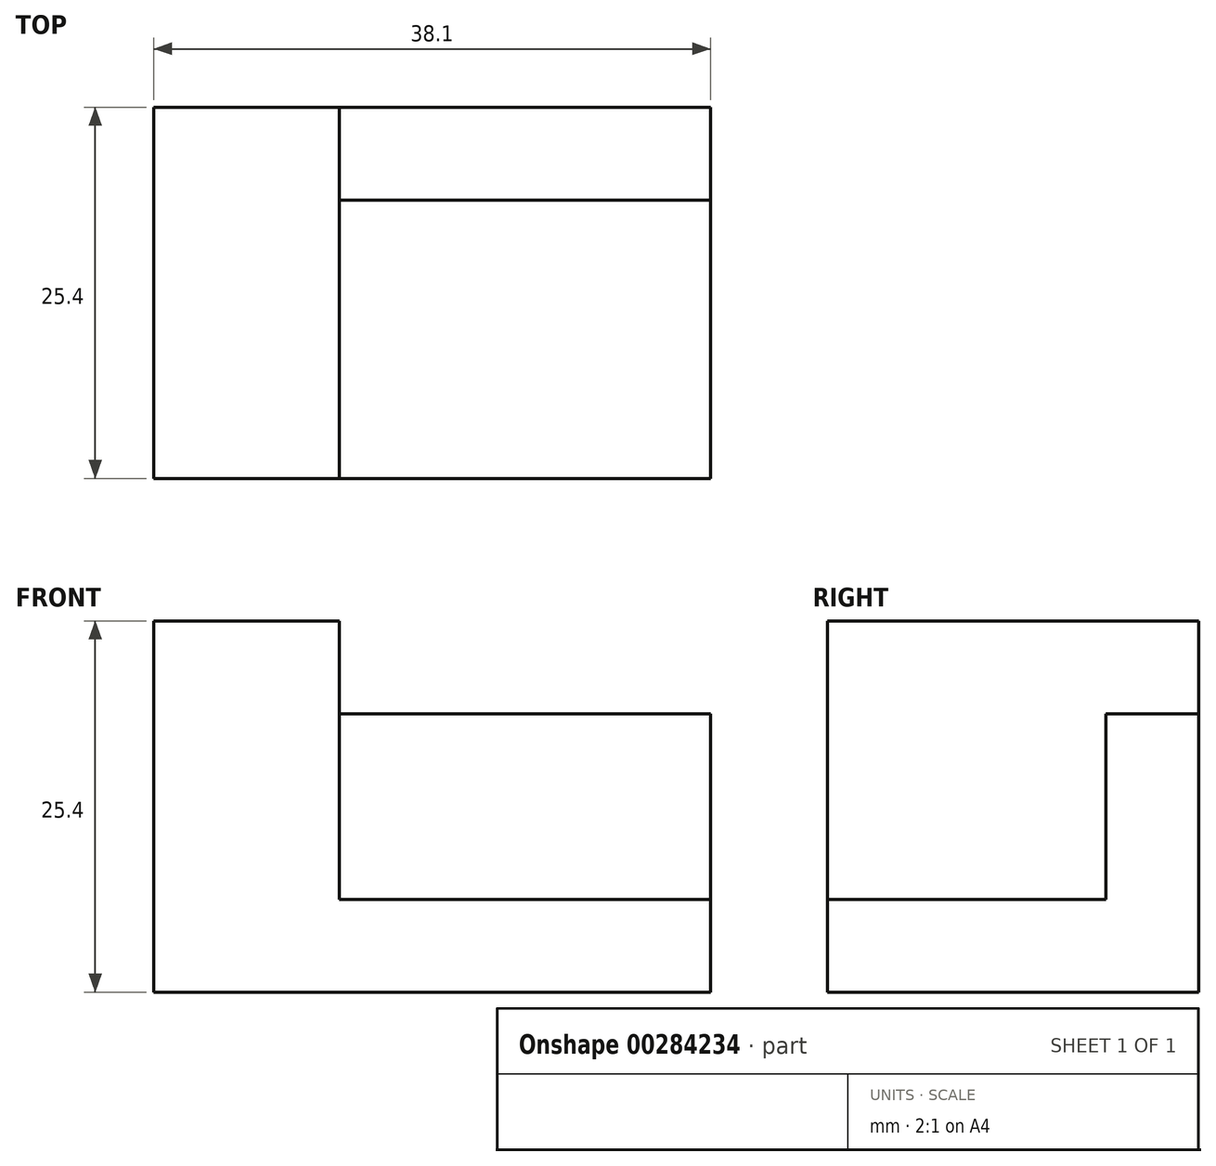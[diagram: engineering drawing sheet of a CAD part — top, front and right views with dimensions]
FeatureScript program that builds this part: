
annotation { "Feature Type Name" : "Feature", "Feature Type Description" : "" }
export const myFeature = defineFeature(function(context is Context, id is Id, definition is map)
    precondition{}
    {
        {
            var Q0;
            Q0=qCreatedBy(makeId("Front.planeOp"),FACE);
            var sketch = newSketch(context, id + "F0", { "sketchPlane" : qUnion([Q0])});
            skLineSegment(sketch, "E0", {"start": v(0, 25.4) * mm, "end": v(0, 0) * mm});
            skLineSegment(sketch, "E1", {"start": v(0, 0) * mm, "end": v(38.1, 0) * mm});
            skLineSegment(sketch, "E2", {"start": v(38.1, 0) * mm, "end": v(38.1, 6.35) * mm});
            skLineSegment(sketch, "E3", {"start": v(38.1, 6.35) * mm, "end": v(12.7, 6.35) * mm});
            skLineSegment(sketch, "E4", {"start": v(12.7, 6.35) * mm, "end": v(12.7, 25.4) * mm});
            skLineSegment(sketch, "E5", {"start": v(12.7, 25.4) * mm, "end": v(0, 25.4) * mm});
            skSolve(sketch);
        }
        {
            var Q0;
            Q0=makeQuery(id+"F0.imprint","IMPRINT",FACE,{"disambiguationData":[TD([[makeQuery(id+"F0.imprint","IMPRINT",EDGE,{"derivedFrom":sQuery(id+"F0.wireOp",EDGE,"E0")}),1.0]])]});
            extrude(context, id + "F1", {"entities" : qUnion([Q0]), "endBound" : BoundingType.SYMMETRIC, "depth" : 25.4 * mm});
        }
        {
            var Q0;
            Q0=makeQuery(id+"F1.opExtrude","SWEPT_FACE",FACE,{"disambiguationData":[OSD([sQuery(id+"F0.wireOp",EDGE,"E3")])]});
            var sketch = newSketch(context, id + "F2", { "sketchPlane" : qUnion([Q0])});
            skLineSegment(sketch, "E6", {"start": v(12.7, 6.35) * mm, "end": v(38.1, 6.35) * mm});
            skLineSegment(sketch, "E7", {"start": v(38.1, 6.35) * mm, "end": v(38.1, 12.7) * mm});
            skLineSegment(sketch, "E8", {"start": v(38.1, 12.7) * mm, "end": v(12.7, 12.7) * mm});
            skLineSegment(sketch, "E9", {"start": v(12.7, 12.7) * mm, "end": v(12.7, 6.35) * mm});
            skSolve(sketch);
        }
        {
            var Q0;
            Q0=makeQuery(id+"F2.imprint","IMPRINT",FACE,{"disambiguationData":[TD([[makeQuery(id+"F2.imprint","IMPRINT",EDGE,{"derivedFrom":sQuery(id+"F2.wireOp",EDGE,"E6")}),1.0]])]});
            extrude(context, id + "F3", {"entities" : qUnion([Q0]), "operationType" : NewBodyOperationType.ADD, "depth" : 12.7 * mm});
        }
    });
